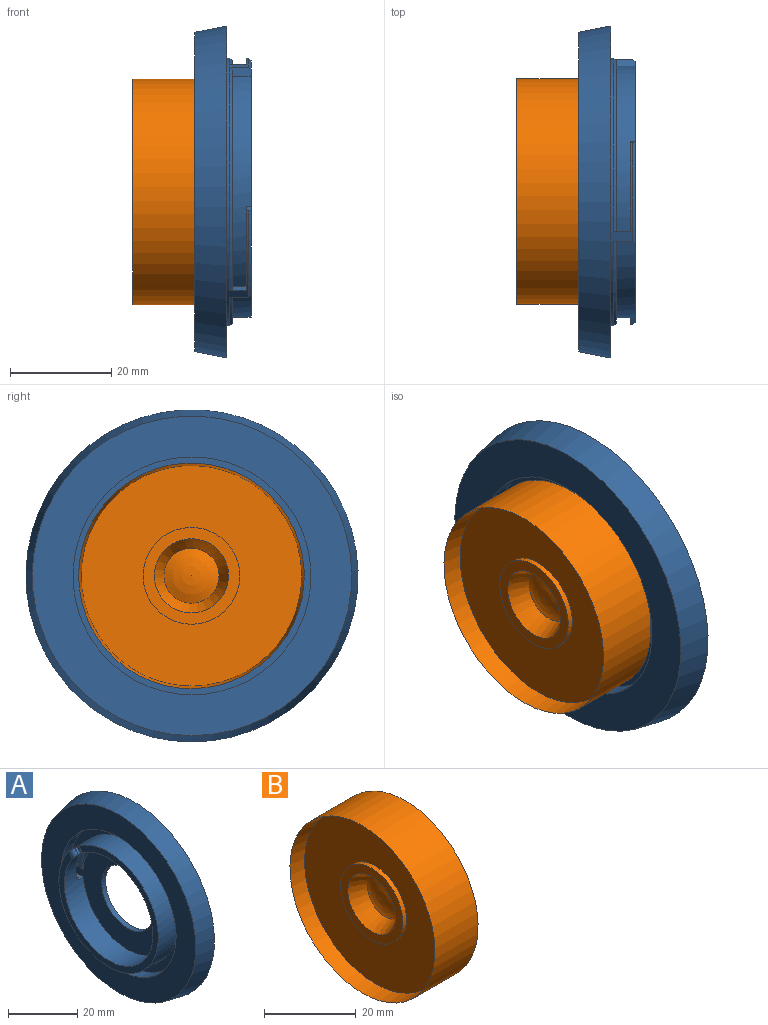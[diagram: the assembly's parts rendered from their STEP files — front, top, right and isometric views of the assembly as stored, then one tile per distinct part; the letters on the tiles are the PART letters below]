
ASSEMBLY  parts=2 mates=1
PART A: 50 faces, bbox 15.3x65.7x65.7 mm
  f0: cylinder r=20.37mm len=40.73mm, axis (1,0,0), area 934.1mm2, adj f7,f8,f39,f40,f41,f42,f43,f44
  f1: cylinder r=18.16mm len=36.33mm, axis (1,0,0), area 830.7mm2, adj f7,f8,f39,f40,f41,f42,f43,f44
  f2: cylinder r=24.89mm len=39.24mm, axis (1,0,0), area 165.9mm2, adj f3,f12,f21,f25,f27,f28
  f3: plane 41.31x21.06mm, normal (1,0,0), area 56.3mm2, adj f2,f21,f25,f33
  f4: cylinder r=24.89mm len=41.51mm, axis (1,0,0), area 165.9mm2, adj f5,f12,f23,f26,f31,f32
  f5: plane 43.29x16.14mm, normal (1,0,0), area 56.3mm2, adj f4,f23,f26,f35
  f6: cylinder r=23.54mm len=47.08mm, axis (1,0,0), area 532.7mm2, adj f8,f20
  f7: plane 40.73x40.73mm, normal (-1,0,0), area 253.5mm2, adj f0,f1,f47,f48
  f8: plane 47.08x47.08mm, normal (-1,0,0), area 1131mm2, adj f0,f1,f6,f9,f43,f44
  f9: cylinder r=10.55mm len=21.1mm, axis (1,0,0), area 106.1mm2, adj f8,f10
  f10: plane 47.08x47.08mm, normal (1,0,0), area 1391mm2, adj f9,f11
  f11: cylinder r=23.54mm len=47.08mm, axis (1,0,0), area 880mm2, adj f10,f12
  f12: plane 51.5x50.88mm, normal (1,0,0), area 272.2mm2, adj f2,f4,f11,f13,f22,f23,f25,f27
  f13: cylinder r=24.89mm len=32.82mm, axis (1,0,0), area 165.9mm2, adj f12,f14,f22,f24,f29,f30
  f14: plane 33.92x29.49mm, normal (1,0,0), area 56.3mm2, adj f13,f22,f24,f34
  f15: cylinder r=26.49mm len=52.98mm, axis (1,0,0), area 964.8mm2, adj f16,f21,f22,f23,f24,f25,f26,f27
  f16: plane 60.58x60.58mm, normal (1,0,0), area 677.8mm2, adj f15,f17
  f17: cone r=31.25mm half-angle=11.1deg, axis (1,0,0), area 966.6mm2, adj f16,f18
  f18: plane 65.7x65.7mm, normal (1,0,0), area 322.2mm2, adj f17,f19
  f19: cone r=31.6mm half-angle=11.1deg, axis (1,0,0), area 1316.1mm2, adj f18,f20
  f20: plane 63.2x63.2mm, normal (-1,0,0), area 1396.4mm2, adj f6,f19
  f21: plane 3.18x1.46mm, normal (0,-0.5,-0.87), area 4.6mm2, adj f2,f3,f15,f28,f33
  f22: plane 4.18x1.5mm, normal (0,0.52,0.85), area 6.5mm2, adj f12,f13,f14,f15,f34,f36
  f23: plane 4.18x1.76mm, normal (0,-1,0.03), area 6.5mm2, adj f4,f5,f12,f15,f35,f37
  f24: plane 3.18x1.68mm, normal (0,1,0), area 4.6mm2, adj f13,f14,f15,f30,f34
  f25: plane 4.18x1.54mm, normal (0,0.48,-0.88), area 6.5mm2, adj f2,f3,f12,f15,f33,f38
  f26: plane 3.18x1.46mm, normal (0,-0.5,0.87), area 4.6mm2, adj f4,f5,f15,f32,f35
  f27: plane 1.54x1mm, normal (0,-0.48,-0.88), area 1.6mm2, adj f2,f12,f15,f28,f36
  f28: plane 15.88x11.01mm, normal (-1,0,0), area 29.1mm2, adj f2,f15,f21,f27
  f29: plane 1.76x1mm, normal (0,1,0.03), area 1.6mm2, adj f12,f13,f15,f30,f37
  f30: plane 17.81x3.64mm, normal (-1,0,0), area 29.1mm2, adj f13,f15,f24,f29
  f31: plane 1.5x1mm, normal (0,-0.52,0.85), area 1.6mm2, adj f4,f12,f15,f32,f38
  f32: plane 16.64x9.75mm, normal (-1,0,0), area 29.1mm2, adj f4,f15,f26,f31
  f33: cone r=25.99mm half-angle=45deg, axis (-1,0,0), area 37.4mm2, adj f3,f15,f21,f25
  f34: cone r=25.99mm half-angle=45deg, axis (-1,0,0), area 37.4mm2, adj f14,f15,f22,f24
  f35: cone r=25.99mm half-angle=45deg, axis (-1,0,0), area 37.4mm2, adj f5,f15,f23,f26
  f36: cone r=26.49mm half-angle=45deg, axis (-1,0,0), area 14.3mm2, adj f12,f15,f22,f27
  f37: cone r=26.49mm half-angle=45deg, axis (-1,0,0), area 14.3mm2, adj f12,f15,f23,f29
  f38: cone r=26.49mm half-angle=45deg, axis (-1,0,0), area 14.3mm2, adj f12,f15,f25,f31
  f39: plane 13.15x7.67mm, normal (-0.98,0.13,-0.13), area 31.3mm2, adj f0,f1,f44,f49
  f40: plane 1.56x1.56mm, normal (0,-0.71,0.71), area 0.2mm2, adj f0,f1,f46,f47
  f41: plane 2.2x1.56mm, normal (0,0.71,-0.71), area 4.9mm2, adj f0,f1,f48,f49
  f42: plane 12.62x5.8mm, normal (0.98,-0.13,0.13), area 28.5mm2, adj f0,f1,f45,f46
  f43: plane 2.21x1.32mm, normal (0,0,1), area 2.6mm2, adj f0,f1,f8,f45
  f44: plane 2.21x0.33mm, normal (0,0,-1), area 0.4mm2, adj f0,f1,f8,f39
  f45: cylinder r=1.45mm len=2.54mm, axis (-0.14,-0.99,0), area 4.6mm2, adj f0,f1,f42,f43
  f46: cylinder r=1.45mm len=2.48mm, axis (0,-0.71,-0.71), area 4.4mm2, adj f0,f1,f40,f42
  f47: cylinder r=1.45mm len=2.71mm, axis (0,0.71,0.71), area 5mm2, adj f0,f1,f7,f40
  f48: cylinder r=1.45mm len=2.71mm, axis (0,-0.71,-0.71), area 5mm2, adj f0,f1,f7,f41
  f49: cylinder r=1.45mm len=2.43mm, axis (0,0.71,0.71), area 4.4mm2, adj f0,f1,f39,f41
PART B: 17 faces, bbox 20.9x44.6x44.6 mm
  f0: cylinder r=20.46mm len=2.72mm, axis (1,0,0), area 5.8mm2, adj f1
  f1: cylinder r=1.36mm len=2.72mm, axis (0,1,0), area 21.3mm2, adj f0,f2
  f2: cylinder r=22.32mm len=2.72mm, axis (1,0,0), area 5.8mm2, adj f1
  f3: cylinder r=20.46mm len=40.93mm, axis (1,0,0), area 1022.3mm2, adj f4,f5
  f4: plane 44.63x44.63mm, normal (1,0,0), area 248.6mm2, adj f3,f6
  f5: plane 40.93x40.93mm, normal (1,0,0), area 642.9mm2, adj f3,f7
  f6: cylinder r=22.32mm len=44.63mm, axis (1,0,0), area 1864.8mm2, adj f4,f8
  f7: cylinder r=14.63mm len=29.27mm, axis (1,0,0), area 466.2mm2, adj f5,f9
  f8: cone r=22.32mm half-angle=7.1deg, axis (-1,0,0), area 561.6mm2, adj f6,f10
  f9: plane 29.27x29.27mm, normal (1,0,0), area 329.8mm2, adj f7,f11
  f10: plane 43.63x43.63mm, normal (-1,0,0), area 1207.3mm2, adj f8,f12
  f11: cylinder r=10.45mm len=20.9mm, axis (1,0,0), area 684.8mm2, adj f9,f13
  f12: cylinder r=9.57mm len=19.14mm, axis (1,0,0), area 69.1mm2, adj f10,f14
  f13: plane 20.9x20.9mm, normal (1,0,0), area 343.1mm2, adj f11
  f14: plane 19.14x19.14mm, normal (-1,0,0), area 118.5mm2, adj f12,f15
  f15: cone r=7.34mm half-angle=24.5deg, axis (-1,0,0), area 182.5mm2, adj f14,f16
  f16: sphere r=13.19mm, area 98.1mm2, adj f15
PLACE A t=(0,-4.32,0.73)mm fixed
PLACE B rot(axis=(-1,0,0),135deg) t=(-2.52,-4.22,0.73)mm
MATE cylindrical B.f0 <-> A.f8  axis (1,0,0) through (-2.52,-4.22,0.73)mm
